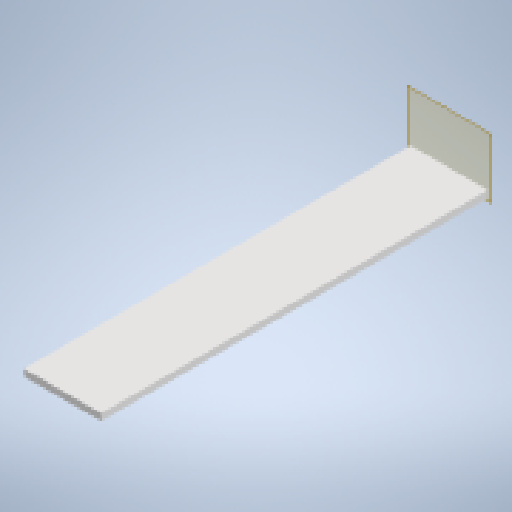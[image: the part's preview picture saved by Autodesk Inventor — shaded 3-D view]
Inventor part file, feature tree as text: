
AUTODESK INVENTOR PART (.ipt)
format: ipt  version: 2023 (Build 270158030, 158C)  size: 146,944 bytes
history: native  units: mm
features: other x4, reference x3, plane x1, extrude x1, sketch x1
ambient origin geometry x8: Origin, YZ Plane, XZ Plane, XY Plane, X Axis, Y Axis, Z Axis, Center Point
bodies: Body1 (feature_tree)
feature tree (10):
  other  "back-plane"
  plane  "Work Plane1"
  extrude  "Extrusion1"  [1 undecoded]
  sketch  "Sketch1"  dims[d0=2030.0mm d1=0.0mm]
  reference  "Reference1"
  reference  "Reference2"
  reference  "Reference3"
  other  "<userpath>\Documents\0004-inventor\3D-CAD-main\primary-engineer-bench.iam"
  other  "primary-engineer-bench.iam"
  other  "bench-end-peice:1"
note: 1 required parameter value undecoded (feature->parameter linkage not recoverable at this tier; creation-order binding heuristic only, values carry confidence <= 0.55)
